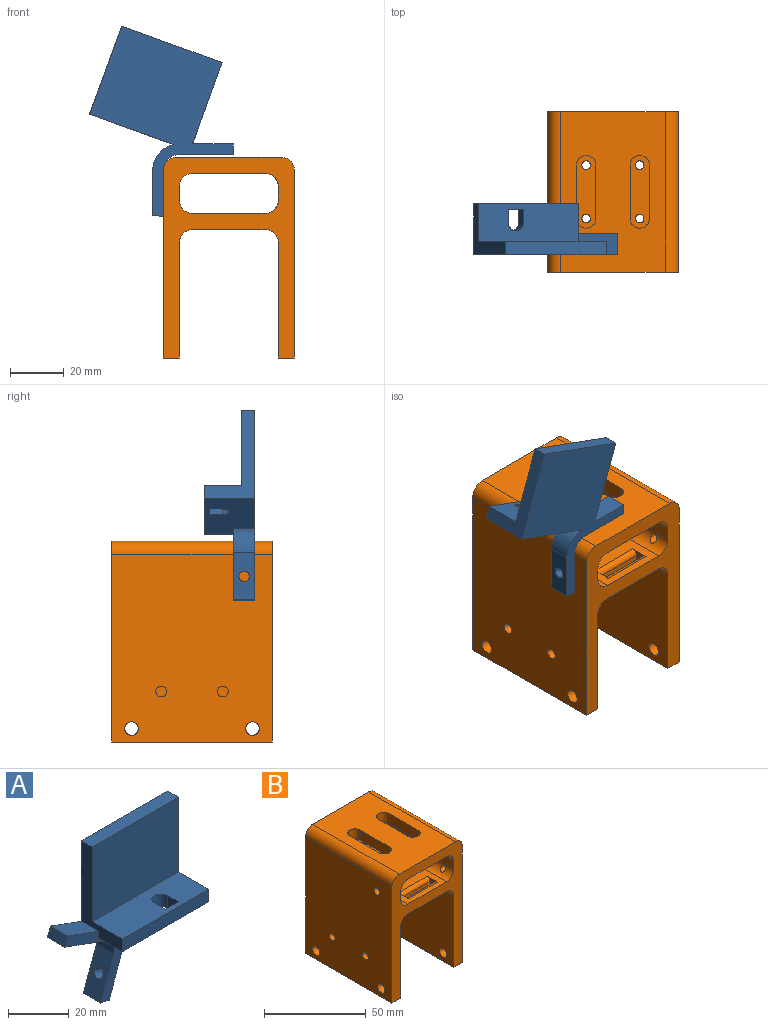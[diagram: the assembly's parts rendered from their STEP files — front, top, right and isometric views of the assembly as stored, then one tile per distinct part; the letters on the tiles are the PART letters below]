
ASSEMBLY  parts=2 mates=1
PART A: 22 faces, bbox 55.7x19x62.5 mm
  f0: plane 35x19mm, normal (-1,0,0), area 223.6mm2, adj f1,f7,f8,f9,f10,f11,f14,f20
  f1: plane 40x5mm, normal (0,-1,0), area 200mm2, adj f0,f6,f7,f8
  f2: plane 6x5mm, normal (0,1,0), area 30mm2, adj f3,f5,f7,f8
  f3: plane 5x5mm, normal (1,0,0), area 25mm2, adj f2,f4,f7,f8
  f4: cylinder r=3mm len=6mm, axis (0,0,-1), area 47.1mm2, adj f3,f5,f7,f8
  f5: plane 5x5mm, normal (-1,0,0), area 25mm2, adj f2,f4,f7,f8
  f6: plane 35x19mm, normal (1,0,0), area 245mm2, adj f1,f7,f8,f9,f10,f11
  f7: plane 40x14mm, normal (0,0,1), area 515.9mm2, adj f0,f1,f2,f3,f4,f5,f6,f9
  f8: plane 40x19mm, normal (0,0,-1), area 662.9mm2, adj f0,f1,f2,f3,f4,f5,f6,f10
  f9: plane 40x30mm, normal (0,-1,0), area 1200mm2, adj f0,f6,f7,f11
  f10: plane 62.46x55.7mm, normal (0,1,0), area 1588.5mm2, adj f0,f6,f8,f11,f12,f13,f14,f15
  f11: plane 40x5mm, normal (0,0,1), area 200mm2, adj f0,f6,f9,f10
  f12: plane 18.97x8mm, normal (-0.34,0,-0.94), area 161.5mm2, adj f10,f13,f19,f20
  f13: plane 8x3.76mm, normal (-0.94,0,0.34), area 32mm2, adj f10,f12,f14,f20
  f14: plane 14.33x8mm, normal (0.34,0,0.94), area 122mm2, adj f0,f10,f13,f20
  f15: cylinder r=10mm len=10.99mm, axis (0,1,0), area 100.8mm2, adj f8,f10,f16,f20
  f16: plane 16.47x8mm, normal (0.94,0,-0.34), area 127.6mm2, adj f10,f15,f17,f20,f21
  f17: plane 8x3.91mm, normal (-0.21,0,-0.98), area 32mm2, adj f10,f16,f18,f20
  f18: plane 16.16x8mm, normal (-0.94,0,0.34), area 125mm2, adj f10,f17,f19,f20,f21
  f19: cylinder r=6mm len=8mm, axis (0,1,0), area 75.4mm2, adj f10,f12,f18,f20
  f20: plane 35.34x26.91mm, normal (0,-1,0), area 188.5mm2, adj f0,f8,f12,f13,f14,f15,f16,f17
  f21: cylinder r=2mm len=5.11mm, axis (0.94,0,-0.34), area 49.8mm2, adj f16,f18
PART B: 65 faces, bbox 49x60x75 mm
  f0: plane 60x39mm, normal (0,0,1), area 1970.6mm2, adj f7,f13,f47,f48,f49,f50,f51,f52
  f1: plane 20x2mm, normal (0,-1,0), area 40mm2, adj f2,f14,f58,f62
  f2: plane 7x6mm, normal (-1,0,0), area 21.4mm2, adj f1,f3,f15,f16,f57,f58,f61,f62
  f3: plane 20x2mm, normal (0,1,0), area 40mm2, adj f2,f14,f57,f61
  f4: plane 7x6mm, normal (-1,0,0), area 21.4mm2, adj f5,f12,f15,f16,f59,f60,f63,f64
  f5: plane 20x2mm, normal (0,1,0), area 40mm2, adj f4,f6,f60,f64
  f6: plane 7x6mm, normal (1,0,0), area 21.4mm2, adj f5,f12,f15,f16,f59,f60,f63,f64
  f7: plane 75x49mm, normal (0,-1,0), area 1365.5mm2, adj f0,f15,f16,f17,f18,f24,f25,f26
  f8: cylinder r=1.6mm len=6mm, axis (0,0,-1), area 60.3mm2, adj f15,f16
  f9: cylinder r=1.6mm len=6mm, axis (0,0,-1), area 60.3mm2, adj f15,f16
  f10: cylinder r=1.6mm len=6mm, axis (0,0,-1), area 60.3mm2, adj f15,f16
  f11: cylinder r=1.6mm len=6mm, axis (0,0,-1), area 60.3mm2, adj f15,f16
  f12: plane 20x2mm, normal (0,-1,0), area 40mm2, adj f4,f6,f59,f63
  f13: plane 75x49mm, normal (0,1,0), area 1365.5mm2, adj f0,f15,f16,f17,f18,f24,f25,f26
  f14: plane 7x6mm, normal (1,0,0), area 21.4mm2, adj f1,f3,f15,f16,f57,f58,f61,f62
  f15: plane 60x27mm, normal (0,0,1), area 1307.8mm2, adj f2,f4,f6,f7,f8,f9,f10,f11
  f16: plane 60x27mm, normal (0,0,-1), area 1307.8mm2, adj f2,f4,f6,f7,f8,f9,f10,f11
  f17: plane 60x5mm, normal (1,0,0), area 287.4mm2, adj f7,f13,f22,f42,f46
  f18: plane 60x6mm, normal (0,0,-1), area 360mm2, adj f7,f13,f24,f25
  f19: cylinder r=2mm len=6mm, axis (1,0,0), area 75.4mm2, adj f24,f25
  f20: cylinder r=2.55mm len=6mm, axis (1,0,0), area 96.1mm2, adj f24,f25
  f21: cylinder r=2.55mm len=6mm, axis (1,0,0), area 96.1mm2, adj f24,f25
  f22: cylinder r=2mm len=6mm, axis (1,0,0), area 75.4mm2, adj f17,f24
  f23: cylinder r=2mm len=6mm, axis (1,0,0), area 75.4mm2, adj f24,f25
  f24: plane 70x60mm, normal (-1,0,0), area 4121.4mm2, adj f7,f13,f18,f19,f20,f21,f22,f23
  f25: plane 60x43mm, normal (1,0,0), area 2514mm2, adj f7,f13,f18,f19,f20,f21,f23,f44
  f26: plane 60x43mm, normal (-1,0,0), area 2539.1mm2, adj f7,f13,f34,f35,f36,f43
  f27: cylinder r=1.5mm len=8mm, axis (-1,0,0), area 64.6mm2, adj f38,f41
  f28: cylinder r=1.5mm len=8mm, axis (-1,0,0), area 64.6mm2, adj f38,f41
  f29: cylinder r=1.5mm len=8mm, axis (-1,0,0), area 64.6mm2, adj f38,f45
  f30: cylinder r=1.5mm len=8mm, axis (-1,0,0), area 64.6mm2, adj f38,f45
  f31: cylinder r=1.5mm len=8mm, axis (-1,0,0), area 64.6mm2, adj f38,f45
  f32: cylinder r=1.5mm len=8mm, axis (-1,0,0), area 64.6mm2, adj f38,f41
  f33: cylinder r=1.5mm len=8mm, axis (-1,0,0), area 64.6mm2, adj f38,f45
  f34: plane 60x6mm, normal (0,0,-1), area 360mm2, adj f7,f13,f26,f38
  f35: cylinder r=2.55mm len=6mm, axis (-1,0,0), area 96.1mm2, adj f26,f38
  f36: cylinder r=2.55mm len=6mm, axis (-1,0,0), area 96.1mm2, adj f26,f38
  f37: cylinder r=1.5mm len=8mm, axis (-1,0,0), area 64.6mm2, adj f38,f41
  f38: plane 70x60mm, normal (1,0,0), area 4102.6mm2, adj f7,f13,f27,f28,f29,f30,f31,f32
  f39: plane 60x5mm, normal (-1,0,0), area 300mm2, adj f7,f13,f41,f45
  f40: plane 60x27mm, normal (0,0,-1), area 1254.8mm2, adj f7,f13,f41,f42,f47,f48,f49,f51
  f41: cylinder r=5mm len=60mm, axis (0,1,0), area 435.3mm2, adj f7,f13,f27,f28,f32,f37,f39,f40
  f42: cylinder r=5mm len=60mm, axis (0,1,0), area 469.2mm2, adj f7,f13,f17,f40,f48,f49,f50
  f43: cylinder r=5mm len=60mm, axis (0,-1,0), area 471.2mm2, adj f7,f13,f16,f26
  f44: cylinder r=5mm len=60mm, axis (0,-1,0), area 471.2mm2, adj f7,f13,f16,f25
  f45: cylinder r=5mm len=60mm, axis (0,1,0), area 437.4mm2, adj f7,f13,f15,f29,f30,f31,f33,f39
  f46: cylinder r=5mm len=60mm, axis (0,1,0), area 471.2mm2, adj f7,f13,f15,f17
  f47: plane 20x6mm, normal (-1,0,0), area 120mm2, adj f0,f40,f48,f49
  f48: cylinder r=3.6mm len=7.2mm, axis (0,0,1), area 67.9mm2, adj f0,f40,f42,f47,f50
  f49: cylinder r=3.6mm len=7.2mm, axis (0,0,1), area 67.9mm2, adj f0,f40,f42,f47,f50
  f50: plane 20x6mm, normal (1,0,0), area 120mm2, adj f0,f42,f48,f49
  f51: plane 20x6mm, normal (1,0,0), area 120mm2, adj f0,f40,f53,f54
  f52: plane 20x6mm, normal (-1,0,0), area 120mm2, adj f0,f41,f53,f54
  f53: cylinder r=3.6mm len=7.2mm, axis (0,0,1), area 67.9mm2, adj f0,f40,f41,f51,f52
  f54: cylinder r=3.6mm len=7.2mm, axis (0,0,1), area 67.9mm2, adj f0,f40,f41,f51,f52
  f55: cylinder r=5mm len=60mm, axis (0,-1,0), area 471.2mm2, adj f0,f7,f13,f38
  f56: cylinder r=5mm len=60mm, axis (0,-1,0), area 471.2mm2, adj f0,f7,f13,f24
  f57: cylinder r=2mm len=20mm, axis (-1,0,0), area 62.8mm2, adj f2,f3,f14,f16
  f58: cylinder r=2mm len=20mm, axis (1,0,0), area 62.8mm2, adj f1,f2,f14,f16
  f59: cylinder r=2mm len=20mm, axis (1,0,0), area 62.8mm2, adj f4,f6,f12,f16
  f60: cylinder r=2mm len=20mm, axis (-1,0,0), area 62.8mm2, adj f4,f5,f6,f16
  f61: cylinder r=2mm len=20mm, axis (1,0,0), area 62.8mm2, adj f2,f3,f14,f15
  f62: cylinder r=2mm len=20mm, axis (-1,0,0), area 62.8mm2, adj f1,f2,f14,f15
  f63: cylinder r=2mm len=20mm, axis (-1,0,0), area 62.8mm2, adj f4,f6,f12,f15
  f64: cylinder r=2mm len=20mm, axis (1,0,0), area 62.8mm2, adj f4,f5,f6,f15
PLACE A rot(axis=(-0.17,0,-0.98),180deg) t=(-46.15,-19.36,59.26)mm
PLACE B t=(-6.77,-16.15,11.61)mm
MATE fastened B.f22 <-> A.f21  axis (-1,0,0) through (-6.27,-5.65,25.49)mm
